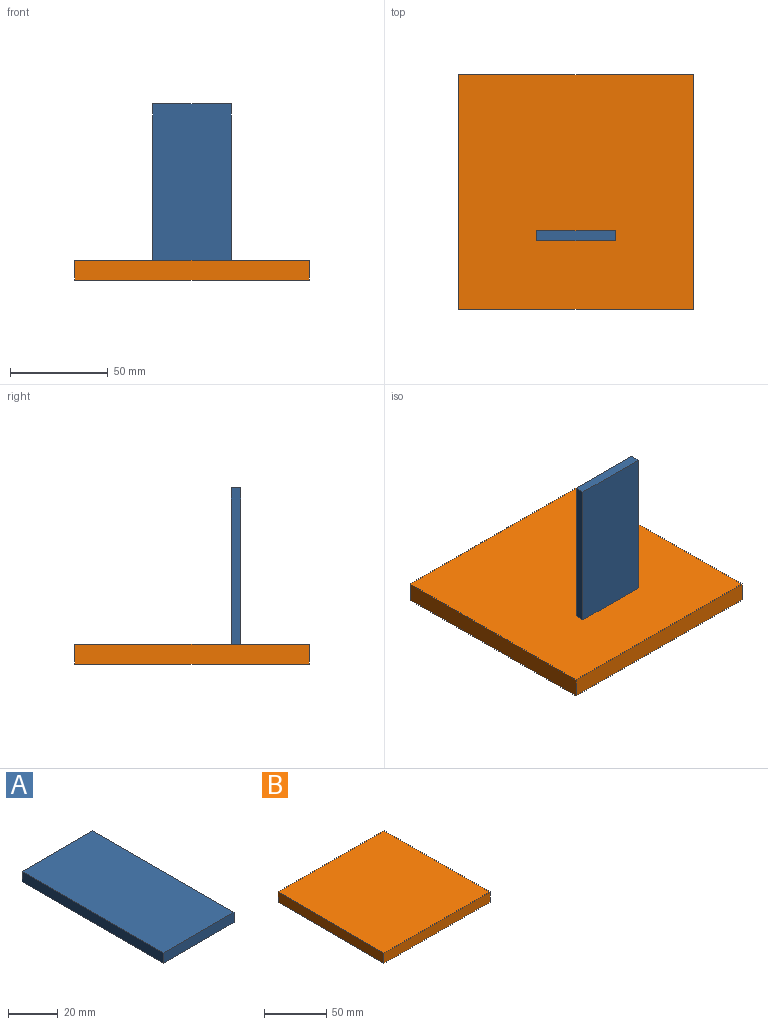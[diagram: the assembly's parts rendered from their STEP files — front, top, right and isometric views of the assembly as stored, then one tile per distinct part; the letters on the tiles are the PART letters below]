
ASSEMBLY  parts=2 mates=1
PART A: 6 faces, bbox 40x80x5 mm
  f0: plane 40x5mm, normal (0,-1,0), area 200mm2, adj f1,f3,f4,f5
  f1: plane 80x5mm, normal (1,0,0), area 400mm2, adj f0,f2,f4,f5
  f2: plane 40x5mm, normal (0,1,0), area 200mm2, adj f1,f3,f4,f5
  f3: plane 80x5mm, normal (-1,0,0), area 400mm2, adj f0,f2,f4,f5
  f4: plane 80x40mm, normal (0,0,1), area 3200mm2, adj f0,f1,f2,f3
  f5: plane 80x40mm, normal (0,0,-1), area 3200mm2, adj f0,f1,f2,f3
PART B: 6 faces, bbox 120x120x10 mm
  f0: plane 120x10mm, normal (-1,0,0), area 1200mm2, adj f1,f3,f4,f5
  f1: plane 120x10mm, normal (0,-1,0), area 1200mm2, adj f0,f2,f4,f5
  f2: plane 120x10mm, normal (1,0,0), area 1200mm2, adj f1,f3,f4,f5
  f3: plane 120x10mm, normal (0,1,0), area 1200mm2, adj f0,f2,f4,f5
  f4: plane 120x120mm, normal (0,0,1), area 14400mm2, adj f0,f1,f2,f3
  f5: plane 120x120mm, normal (0,0,-1), area 14400mm2, adj f0,f1,f2,f3
PLACE A rot(axis=(1,0,0),90deg) t=(-10.07,-32.85,69.46)mm
PLACE B t=(-10.07,-12.85,19.46)mm fixed
MATE fastened A.f0 <-> B.f4  axis (0,0,-1) through (-10.07,-32.85,29.46)mm
